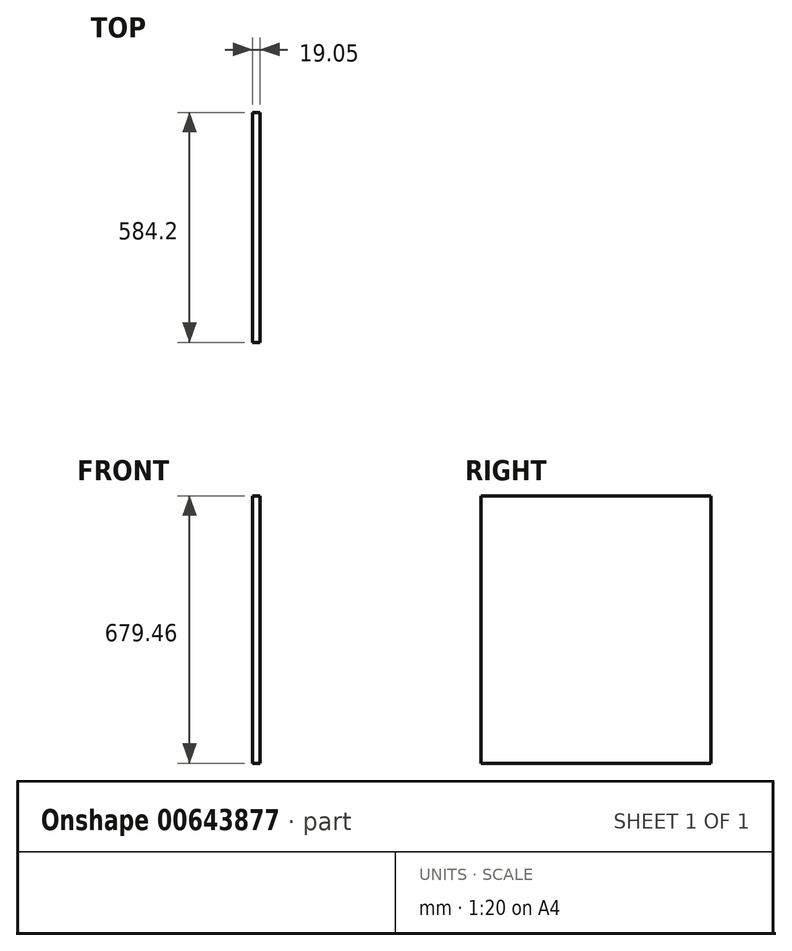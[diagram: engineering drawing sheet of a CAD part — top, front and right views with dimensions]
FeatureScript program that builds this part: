
annotation { "Feature Type Name" : "Feature", "Feature Type Description" : "" }
export const myFeature = defineFeature(function(context is Context, id is Id, definition is map)
    precondition{}
    {
        {
            var Q0;
            Q0=qCreatedBy(makeId("Right.planeOp"),FACE);
            var sketch = newSketch(context, id + "F0", { "sketchPlane" : qUnion([Q0])});
            skLineSegment(sketch, "E0.bottom", {"start": v(292.1, 339.73) * mm, "end": v(-292.1, 339.73) * mm});
            skLineSegment(sketch, "E0.top", {"start": v(292.1, -339.73) * mm, "end": v(-292.1, -339.73) * mm});
            skLineSegment(sketch, "E0.left", {"start": v(292.1, 339.73) * mm, "end": v(292.1, -339.73) * mm});
            skLineSegment(sketch, "E0.right", {"start": v(-292.1, 339.73) * mm, "end": v(-292.1, -339.73) * mm});
            skPoint(sketch, "E0.middle", {"position": v(0, 0) * mm});
            skSolve(sketch);
        }
        {
            var Q0;
            Q0=makeQuery(id+"F0.imprint","IMPRINT",FACE,{"disambiguationData":[TD([[makeQuery(id+"F0.imprint","IMPRINT",EDGE,{"derivedFrom":sQuery(id+"F0.wireOp",EDGE,"E0.bottom")}),1.0]])]});
            extrude(context, id + "F1", {"entities" : qUnion([Q0]), "depth" : 19.05 * mm, "offsetDistance" : 25.4 * mm});
        }
    });
